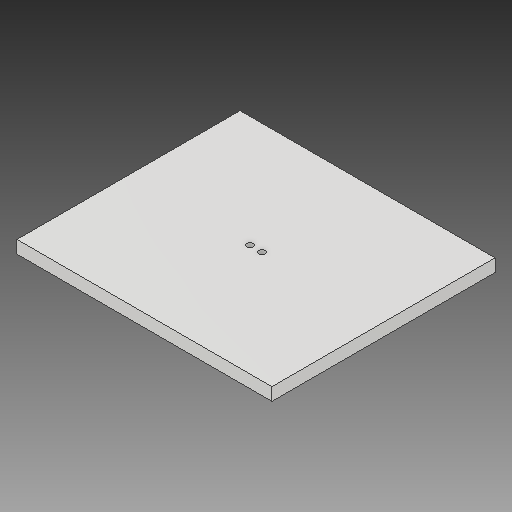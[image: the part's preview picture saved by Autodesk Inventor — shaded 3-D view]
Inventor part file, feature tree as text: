
AUTODESK INVENTOR PART (.ipt)
format: ipt  version: 2018.1 (Build 221171000, 171)  size: 112,128 bytes
history: native  units: mm
features: other x4, extrude x3, sketch x3, reference x2
ambient origin geometry x8: Origin, YZ Plane, XZ Plane, XY Plane, X Axis, Y Axis, Z Axis, Center Point
bodies: Solid1 (feature_tree)
feature tree (12):
  parser-record x2  (decoder bookkeeping rows leaked as tree rows — omitted from the tree; the rows remain in map.json)
  extrude  "Extrusion1"  Depth=350.0mm
  extrude  "Extrusion2"  Depth=20.0mm TaperAngle=0.0deg
  extrude  "Extrusion4"  Depth=10.0mm
  sketch  "Sketch1"  dims[d0=400.0mm d1=350.0mm]
  sketch  "Sketch2"  dims[d2=20.0mm d3=0.0mm d4=20.0mm d5=0.0mm]
  reference  "Reference1"
  reference  "Reference2"
  sketch  "Sketch4"  dims[d10=10.0mm d11=10.0mm d12=6.0mm d13=0.0mm]
  other  "load cell_assembly.iam"
  other  "load cell:1"
note: 2 file-system paths scrubbed to <path> (originals preserved in map.json)
